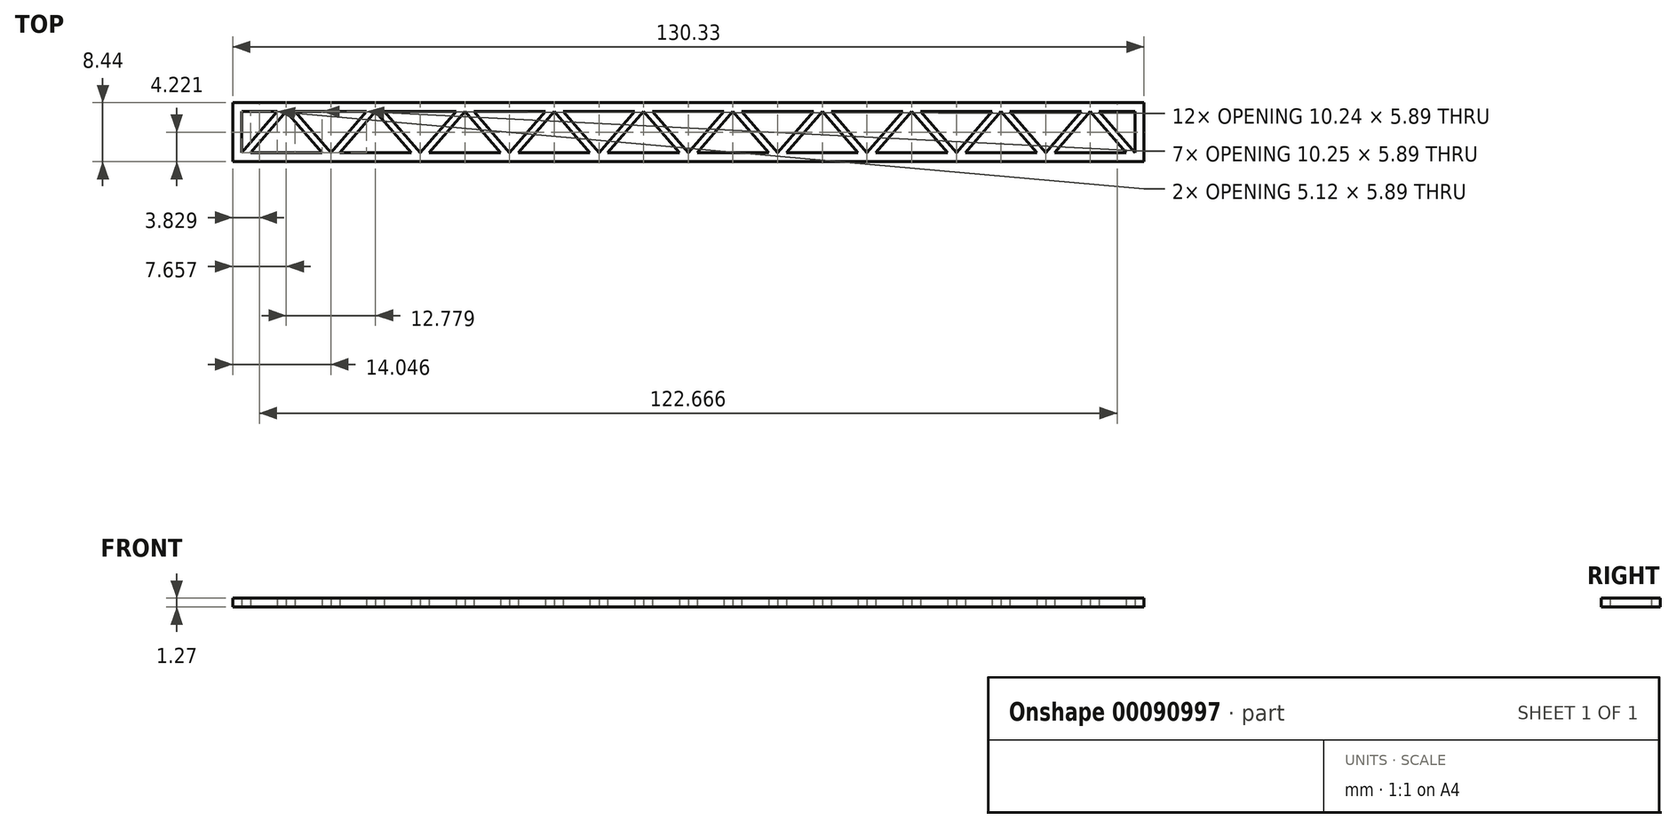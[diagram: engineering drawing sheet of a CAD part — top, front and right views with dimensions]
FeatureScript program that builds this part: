
annotation { "Feature Type Name" : "Feature", "Feature Type Description" : "" }
export const myFeature = defineFeature(function(context is Context, id is Id, definition is map)
    precondition{}
    {
        {
            var Q0;
            Q0=qCreatedBy(makeId("Top.planeOp"),FACE);
            var sketch = newSketch(context, id + "F0", { "sketchPlane" : qUnion([Q0])});
            skLineSegment(sketch, "E0.bottom", {"start": v(-111.28, 4.95) * mm, "end": v(19.05, 4.95) * mm});
            skLineSegment(sketch, "E0.top", {"start": v(-111.28, -3.49) * mm, "end": v(19.05, -3.49) * mm});
            skLineSegment(sketch, "E0.left", {"start": v(-111.28, 4.95) * mm, "end": v(-111.28, -3.49) * mm});
            skLineSegment(sketch, "E1.bottom", {"start": v(-110.01, 3.68) * mm, "end": v(-104.9, 3.68) * mm});
            skLineSegment(sketch, "E1.top", {"start": v(-108.74, -2.22) * mm, "end": v(-98.5, -2.22) * mm});
            skLineSegment(sketch, "E1.left", {"start": v(-110.01, 3.68) * mm, "end": v(-110.01, -2.22) * mm});
            skLineSegment(sketch, "E2", {"start": v(-110.01, -2.22) * mm, "end": v(-104.9, 3.68) * mm});
            skLineSegment(sketch, "E3", {"start": v(-103.62, 3.68) * mm, "end": v(-108.74, -2.22) * mm});
            skLineSegment(sketch, "E4.MirrorCS", {"start": v(-103.62, 3.68) * mm, "end": v(-98.5, -2.22) * mm});
            skLineSegment(sketch, "E5.MirrorCS", {"start": v(-97.23, -2.22) * mm, "end": v(-102.36, 3.68) * mm});
            skLineSegment(sketch, "E6.trimOffspring", {"start": v(-102.36, 3.68) * mm, "end": v(-92.11, 3.68) * mm});
            skLineSegment(sketch, "E7.trimOffspring", {"start": v(-95.96, -2.22) * mm, "end": v(-85.73, -2.22) * mm});
            skLineSegment(sketch, "E8.MirrorCS", {"start": v(-97.23, -2.22) * mm, "end": v(-92.11, 3.68) * mm});
            skLineSegment(sketch, "E9.MirrorCS", {"start": v(-90.84, 3.68) * mm, "end": v(-95.96, -2.22) * mm});
            skLineSegment(sketch, "E10.MirrorCS", {"start": v(-90.84, 3.68) * mm, "end": v(-85.73, -2.22) * mm});
            skLineSegment(sketch, "E11.MirrorCS", {"start": v(-84.46, -2.22) * mm, "end": v(-89.58, 3.68) * mm});
            skLineSegment(sketch, "E12.trimOffspring", {"start": v(-83.19, -2.22) * mm, "end": v(-72.95, -2.22) * mm});
            skLineSegment(sketch, "E13.trimOffspring", {"start": v(-89.58, 3.68) * mm, "end": v(-79.33, 3.68) * mm});
            skLineSegment(sketch, "E14.MirrorCS", {"start": v(-84.46, -2.22) * mm, "end": v(-79.33, 3.68) * mm});
            skLineSegment(sketch, "E15.MirrorCS", {"start": v(-78.07, 3.68) * mm, "end": v(-83.19, -2.22) * mm});
            skLineSegment(sketch, "E16.MirrorCS", {"start": v(-78.07, 3.68) * mm, "end": v(-72.95, -2.22) * mm});
            skLineSegment(sketch, "E17.MirrorCS", {"start": v(-71.68, -2.22) * mm, "end": v(-76.8, 3.68) * mm});
            skLineSegment(sketch, "E18.MirrorCS", {"start": v(-71.68, -2.22) * mm, "end": v(-66.55, 3.68) * mm});
            skLineSegment(sketch, "E19.MirrorCS", {"start": v(-65.29, 3.68) * mm, "end": v(-70.4, -2.22) * mm});
            skLineSegment(sketch, "E20.MirrorCS", {"start": v(-65.29, 3.68) * mm, "end": v(-60.17, -2.22) * mm});
            skLineSegment(sketch, "E21.MirrorCS", {"start": v(-58.9, -2.22) * mm, "end": v(-64.02, 3.68) * mm});
            skLineSegment(sketch, "E22.trimOffspring", {"start": v(-76.8, 3.68) * mm, "end": v(-66.55, 3.68) * mm});
            skLineSegment(sketch, "E23.trimOffspring", {"start": v(-70.4, -2.22) * mm, "end": v(-60.17, -2.22) * mm});
            skLineSegment(sketch, "E24.trimOffspring", {"start": v(-64.02, 3.68) * mm, "end": v(-53.77, 3.68) * mm});
            skLineSegment(sketch, "E25.trimOffspring", {"start": v(-57.63, -2.22) * mm, "end": v(-47.39, -2.22) * mm});
            skLineSegment(sketch, "E26.MirrorCS", {"start": v(-58.9, -2.22) * mm, "end": v(-53.77, 3.68) * mm});
            skLineSegment(sketch, "E27.MirrorCS", {"start": v(-52.5, 3.68) * mm, "end": v(-57.63, -2.22) * mm});
            skLineSegment(sketch, "E28.MirrorCS", {"start": v(-52.5, 3.68) * mm, "end": v(-47.39, -2.22) * mm});
            skLineSegment(sketch, "E29.MirrorCS", {"start": v(-46.12, -2.22) * mm, "end": v(-51.24, 3.68) * mm});
            skLineSegment(sketch, "E30.MirrorCS", {"start": v(-46.12, -2.22) * mm, "end": v(-41, 3.68) * mm});
            skLineSegment(sketch, "E31.MirrorCS", {"start": v(-39.73, 3.68) * mm, "end": v(-44.85, -2.22) * mm});
            skLineSegment(sketch, "E32.MirrorCS", {"start": v(-39.73, 3.68) * mm, "end": v(-34.6, -2.22) * mm});
            skLineSegment(sketch, "E33.MirrorCS", {"start": v(-33.34, -2.22) * mm, "end": v(-38.46, 3.68) * mm});
            skLineSegment(sketch, "E34.MirrorCS", {"start": v(-33.34, -2.22) * mm, "end": v(-28.22, 3.68) * mm});
            skLineSegment(sketch, "E35.MirrorCS", {"start": v(-26.95, 3.68) * mm, "end": v(-32.07, -2.22) * mm});
            skLineSegment(sketch, "E36.MirrorCS", {"start": v(-26.95, 3.68) * mm, "end": v(-21.83, -2.22) * mm});
            skLineSegment(sketch, "E37.MirrorCS", {"start": v(-20.56, -2.22) * mm, "end": v(-25.68, 3.68) * mm});
            skLineSegment(sketch, "E38.MirrorCS", {"start": v(-20.56, -2.22) * mm, "end": v(-15.44, 3.68) * mm});
            skLineSegment(sketch, "E39.MirrorCS", {"start": v(-14.17, 3.68) * mm, "end": v(-19.3, -2.22) * mm});
            skLineSegment(sketch, "E40.MirrorCS", {"start": v(-14.17, 3.68) * mm, "end": v(-9.05, -2.22) * mm});
            skLineSegment(sketch, "E41.MirrorCS", {"start": v(-7.78, -2.22) * mm, "end": v(-12.9, 3.68) * mm});
            skLineSegment(sketch, "E42.trimOffspring", {"start": v(-51.24, 3.68) * mm, "end": v(-41, 3.68) * mm});
            skLineSegment(sketch, "E43.trimOffspring", {"start": v(-44.85, -2.22) * mm, "end": v(-34.6, -2.22) * mm});
            skLineSegment(sketch, "E44.trimOffspring", {"start": v(-38.46, 3.68) * mm, "end": v(-28.22, 3.68) * mm});
            skLineSegment(sketch, "E45.trimOffspring", {"start": v(-32.07, -2.22) * mm, "end": v(-21.83, -2.22) * mm});
            skLineSegment(sketch, "E46.trimOffspring", {"start": v(-25.68, 3.68) * mm, "end": v(-15.44, 3.68) * mm});
            skLineSegment(sketch, "E47.trimOffspring", {"start": v(-19.3, -2.22) * mm, "end": v(-9.05, -2.22) * mm});
            skLineSegment(sketch, "E48.trimOffspring", {"start": v(-12.9, 3.68) * mm, "end": v(-2.66, 3.68) * mm});
            skLineSegment(sketch, "E49.trimOffspring", {"start": v(-6.51, -2.22) * mm, "end": v(3.73, -2.22) * mm});
            skLineSegment(sketch, "E50.MirrorCS", {"start": v(-7.78, -2.22) * mm, "end": v(-2.66, 3.68) * mm});
            skLineSegment(sketch, "E51.MirrorCS", {"start": v(-1.4, 3.68) * mm, "end": v(-6.51, -2.22) * mm});
            skLineSegment(sketch, "E52.MirrorCS", {"start": v(-1.4, 3.68) * mm, "end": v(3.73, -2.22) * mm});
            skLineSegment(sketch, "E53.MirrorCS", {"start": v(5, -2.22) * mm, "end": v(-0.13, 3.68) * mm});
            skLineSegment(sketch, "E54.MirrorCS", {"start": v(5, -2.22) * mm, "end": v(10.12, 3.68) * mm});
            skLineSegment(sketch, "E55.MirrorCS", {"start": v(11.39, 3.68) * mm, "end": v(6.27, -2.22) * mm});
            skLineSegment(sketch, "E56.MirrorCS", {"start": v(11.39, 3.68) * mm, "end": v(16.5, -2.22) * mm});
            skLineSegment(sketch, "E57.MirrorCS", {"start": v(17.78, -2.22) * mm, "end": v(12.65, 3.68) * mm});
            skLineSegment(sketch, "E58.trimOffspring", {"start": v(12.65, 3.68) * mm, "end": v(17.78, 3.68) * mm});
            skLineSegment(sketch, "E59.trimOffspring", {"start": v(6.27, -2.22) * mm, "end": v(16.5, -2.22) * mm});
            skLineSegment(sketch, "E60.trimOffspring", {"start": v(-0.13, 3.68) * mm, "end": v(10.12, 3.68) * mm});
            skLineSegment(sketch, "E61", {"start": v(17.78, -2.22) * mm, "end": v(17.78, 3.68) * mm});
            skPoint(sketch, "E61.endSnap0", {"position": v(17.78, 3.68) * mm});
            skLineSegment(sketch, "E62", {"start": v(17.78, 3.68) * mm, "end": v(17.78, -2.22) * mm});
            skLineSegment(sketch, "E63", {"start": v(19.05, -2.22) * mm, "end": v(19.05, -3.49) * mm});
            skLineSegment(sketch, "E64", {"start": v(19.05, -3.49) * mm, "end": v(19.05, 4.95) * mm});
            skPoint(sketch, "E65.orphan", {"position": v(17.78, 4.95) * mm});
            skPoint(sketch, "E66.MirrorCS.end.orphan", {"position": v(22.9, 3.68) * mm});
            skSolve(sketch);
        }
        {
            var Q0;
            Q0 = qSketchRegion(id + "F0", true);
            extrude(context, id + "F1", {"entities" : qUnion([Q0]), "depth" : 1.27 * mm});
        }
    });
